# Revit family: Toilet-Floor_Mount-KOHLER-Cimarron_Comfort_Height-K-31624
name_source: partatom
category: Plumbing Fixtures
units: mm (PartAtom-declared; Revit-internal decimal feet)

## family parameters
Cut with Voids When Loaded = No
Host = Face
Maintain Annotation Orientation = No
OmniClass Number = 23.31.19.00
Part Type = Normal
Room Calculation Point = No
Round Connector Dimension = Use Diameter
Shared = No

## types (6) — shared parameters
ADA Compliant = Yes
Assembly Code = D2010100
CW Connection = Yes
Cold Water Inlet = Cold Water Inlet
Date Modified = 01/20/2022
Default Elevation = 0"
Description = Two-piece elongated 1.28 gpf toilet with Revolution 360 and ContinuousClean technologies
Flow Rate = 0 GPM
Flush Rate- GPF = 1.28 GPF
Flush Rate- LPF = 4.8 LPF
HW Connection = No
Height = 31 1/4"
Hot Water Inlet = Hot Water Inlet
Length = 28 15/16"
Manufacturer = KOHLER Co.
Master Format 2014 = 22 42 13.13
Master Format 2014 Name = Residential Water Closets
Material = VITERIOUS CHINA
Pressure = 0.00 psi
Product Documentation Link = https://www.us.kohler.com
Product Name = Cimarron Comfort Height
Product Page URL = http://www.us.kohler.com
Rough-In = 12"
Seat Included = No
URL = https://www.us.kohler.com
Vent Connection = No
Waste Connection = Yes
Waste Water Outlet = Waste Water Outlet
WaterSense Certified = Yes
Width = 18 5/8"

## per-type parameters (varying)
| type | Finish | Model | Type |
| 0-White | Kohler-Vitreous_China-0-White | K-31624-0 | 1 |
| 7-Black Black | Kohler-Vitreous_China-7-Black_Black | K-31624-7 | 2 |
| 95-Ice Grey | Kohler-Vitreous_China-95-Ice_Grey | K-31624-95 | 3 |
| 96-Biscuit | Kohler-Vitreous_China-96-Biscuit | K-31624-96 | 4 |
| G9-Sandbar | Kohler-Vitreous_China-G9-Sandbar | K-31624-G9 | 5 |
| NY-Dune | Kohler-Vitreous_China-NY-Dune | K-31624-NY | 6 |

## geometry (parser evidence)
native form markers: Sweep x5
no freeform markers — native parametric forms only
